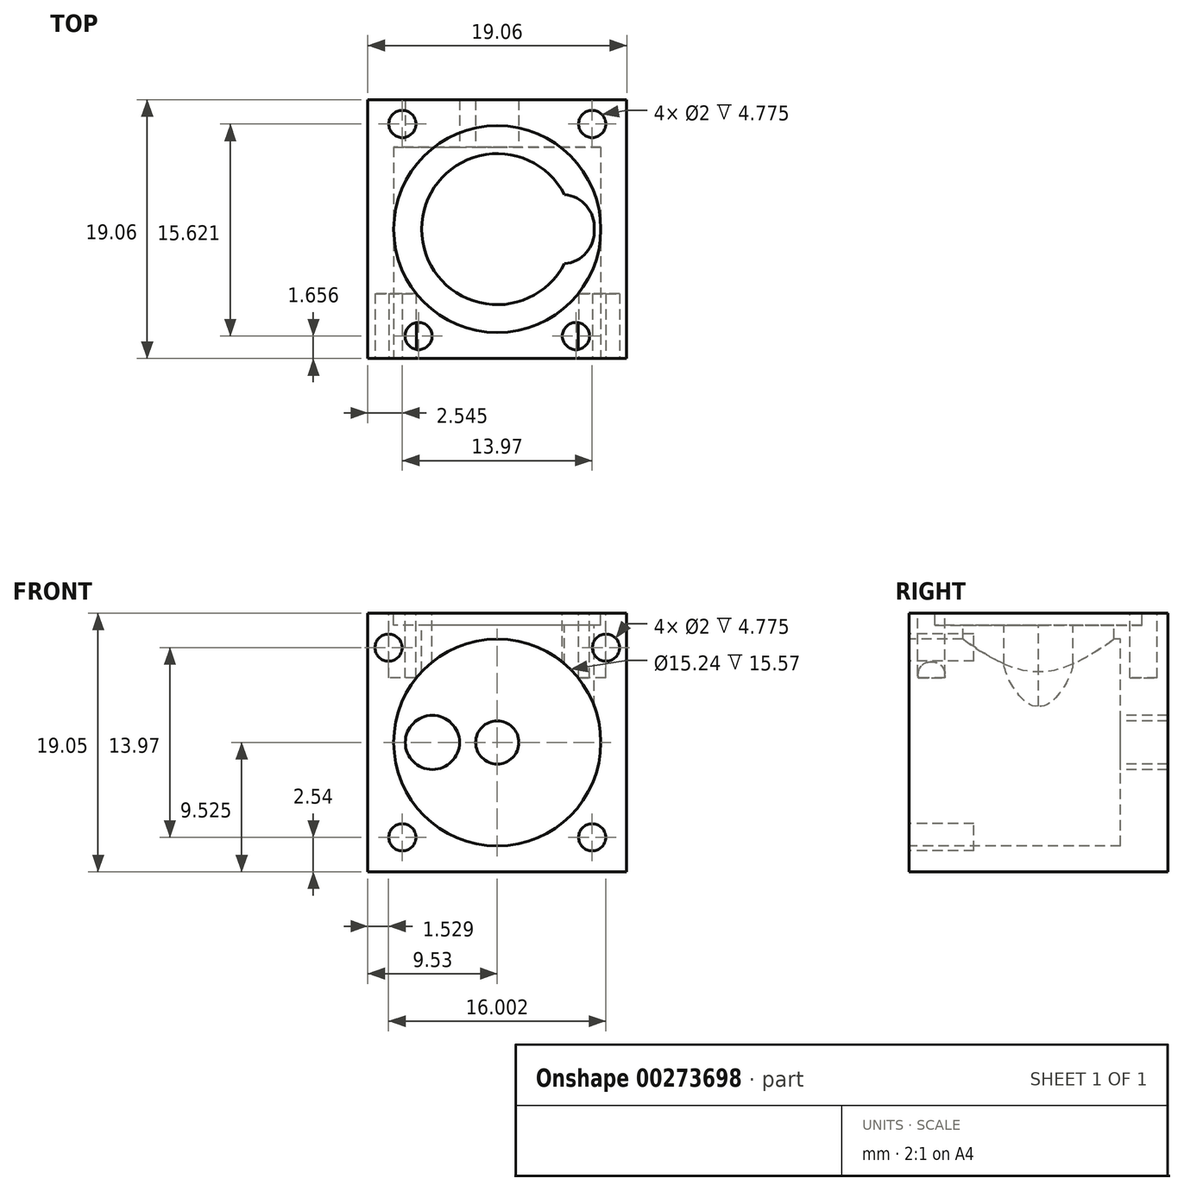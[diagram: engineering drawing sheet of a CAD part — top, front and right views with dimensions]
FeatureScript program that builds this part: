
annotation { "Feature Type Name" : "Feature", "Feature Type Description" : "" }
export const myFeature = defineFeature(function(context is Context, id is Id, definition is map)
    precondition{}
    {
        {
            var Q0;
            Q0=qCreatedBy(makeId("Top.planeOp"),FACE);
            var sketch = newSketch(context, id + "F0", { "sketchPlane" : qUnion([Q0])});
            skLineSegment(sketch, "E0.bottom", {"start": v(9.53, -9.52) * mm, "end": v(-9.53, -9.53) * mm});
            skLineSegment(sketch, "E0.top", {"start": v(9.53, 9.53) * mm, "end": v(-9.53, 9.52) * mm});
            skLineSegment(sketch, "E0.left", {"start": v(9.53, -9.52) * mm, "end": v(9.53, 9.53) * mm});
            skLineSegment(sketch, "E0.right", {"start": v(-9.53, -9.53) * mm, "end": v(-9.53, 9.52) * mm});
            skPoint(sketch, "E0.middle", {"position": v(0, 0) * mm});
            skSolve(sketch);
        }
        {
            var Q0;
            Q0 = qSketchRegion(id + "F0", true);
            extrude(context, id + "F1", {"entities" : qUnion([Q0]), "depth" : 19.05 * mm});
        }
        {
            var Q0;
            Q0=makeQuery(id+"F1.opExtrude","CAP_FACE",FACE,{"disambiguationData":[OSD([sQuery(id+"F0.wireOp",EDGE,"E0.bottom"),sQuery(id+"F0.wireOp",EDGE,"E0.top"),sQuery(id+"F0.wireOp",EDGE,"E0.left"),sQuery(id+"F0.wireOp",EDGE,"E0.right")])],"isStart":false});
            var sketch = newSketch(context, id + "F2", { "sketchPlane" : qUnion([Q0])});
            skCircle(sketch, "E1", {"center": v(0, 0) * mm, "radius": 7.62 * mm});
            skArc(sketch, "E2", {"start": v(4.95, 2.54) * mm, "mid": v(-5.56, 0) * mm, "end": v(4.95, -2.54) * mm});
            skCircle(sketch, "E3", {"center": v(-5.8, -7.87) * mm, "radius": 1 * mm, "construction": true});
            skCircle(sketch, "E4", {"center": v(-6.99, 7.75) * mm, "radius": 1 * mm, "construction": true});
            skCircle(sketch, "E5", {"center": v(5.8, -7.87) * mm, "radius": 1 * mm, "construction": true});
            skCircle(sketch, "E6", {"center": v(6.99, 7.75) * mm, "radius": 1 * mm, "construction": true});
            skArc(sketch, "E7", {"start": v(4.95, -2.54) * mm, "mid": v(6.56, -1.72) * mm, "end": v(7.13, 0) * mm});
            skArc(sketch, "E8", {"start": v(7.13, 0) * mm, "mid": v(6.56, 1.72) * mm, "end": v(4.95, 2.54) * mm});
            skSolve(sketch);
        }
        {
            var Q0;
            Q0 = qSketchRegion(id + "F2", true);
            extrude(context, id + "F3", {"entities" : qUnion([Q0]), "operationType" : NewBodyOperationType.REMOVE, "oppositeDirection" : true, "depth" : 0.89 * mm});
        }
        {
            var Q0;
            Q0=makeQuery(id+"F2.imprint","IMPRINT",FACE,{"disambiguationData":[TD([[makeQuery(id+"F2.imprint","IMPRINT",EDGE,{"derivedFrom":sQuery(id+"F2.wireOp",EDGE,"E1")}),-1.0]])]});
            var sketch = newSketch(context, id + "F4", { "sketchPlane" : qUnion([Q0])});
            skCircle(sketch, "E9.0", {"center": v(-5.8, -7.87) * mm, "radius": 1 * mm});
            skCircle(sketch, "E10.0", {"center": v(5.8, -7.87) * mm, "radius": 1 * mm});
            skCircle(sketch, "E11.0", {"center": v(6.99, 7.75) * mm, "radius": 1 * mm});
            skCircle(sketch, "E12.0", {"center": v(-6.99, 7.75) * mm, "radius": 1 * mm});
            skSolve(sketch);
        }
        {
            var Q0;
            Q0 = qSketchRegion(id + "F4", true);
            extrude(context, id + "F5", {"entities" : qUnion([Q0]), "operationType" : NewBodyOperationType.REMOVE, "oppositeDirection" : true, "depth" : 4.78 * mm});
        }
        {
            var Q0;
            Q0=makeQuery(id+"F1.opExtrude","SWEPT_FACE",FACE,{"disambiguationData":[OSD([sQuery(id+"F0.wireOp",EDGE,"E0.bottom")])]});
            var sketch = newSketch(context, id + "F6", { "sketchPlane" : qUnion([Q0])});
            skLineSegment(sketch, "E13", {"start": v(-9.53, 19.05) * mm, "end": v(9.53, 0) * mm, "construction": true});
            skLineSegment(sketch, "E14", {"start": v(9.53, 19.05) * mm, "end": v(-9.53, 0) * mm, "construction": true});
            skPoint(sketch, "E15", {"position": v(0, 9.53) * mm});
            skCircle(sketch, "E16", {"center": v(0, 9.53) * mm, "radius": 7.62 * mm});
            skSolve(sketch);
        }
        {
            var Q0;
            Q0 = qSketchRegion(id + "F6", true);
            extrude(context, id + "F7", {"entities" : qUnion([Q0]), "operationType" : NewBodyOperationType.REMOVE, "oppositeDirection" : true, "depth" : 15.57 * mm});
        }
        {
            var Q0;
            Q0=makeQuery(id+"F3.boolean.opBoolean","SPLIT",FACE,{"disambiguationData":[TD([makeQuery(id+"F3.opExtrude","SWEPT_FACE",FACE,{"disambiguationData":[OSD([sQuery(id+"F2.wireOp",EDGE,"E2")])]})])],"derivedFrom":makeQuery(id+"F1.opExtrude","CAP_FACE",FACE,{"disambiguationData":[OSD([sQuery(id+"F0.wireOp",EDGE,"E0.bottom"),sQuery(id+"F0.wireOp",EDGE,"E0.top"),sQuery(id+"F0.wireOp",EDGE,"E0.left"),sQuery(id+"F0.wireOp",EDGE,"E0.right")])],"isStart":false})});
            var sketch = newSketch(context, id + "F8", { "sketchPlane" : qUnion([Q0])});
            skArc(sketch, "E17.0.0", {"start": v(4.95, -2.54) * mm, "mid": v(6.56, -1.72) * mm, "end": v(7.13, 0) * mm});
            skArc(sketch, "E17.0.1", {"start": v(7.13, 0) * mm, "mid": v(6.56, 1.72) * mm, "end": v(4.95, 2.54) * mm});
            skArc(sketch, "E17.0.2", {"start": v(4.95, 2.54) * mm, "mid": v(-5.56, 0) * mm, "end": v(4.95, -2.54) * mm});
            skSolve(sketch);
        }
        {
            var Q0;
            Q0 = qSketchRegion(id + "F8", true);
            extrude(context, id + "F9", {"entities" : qUnion([Q0]), "operationType" : NewBodyOperationType.REMOVE, "endBound" : BoundingType.UP_TO_NEXT, "oppositeDirection" : true, "depth" : 25.4 * mm});
        }
        {
            var Q0;
            Q0=makeQuery(id+"F7.boolean.opBoolean","COPY",FACE,{"derivedFrom":makeQuery(id+"F7.opExtrude","CAP_FACE",FACE,{"disambiguationData":[OSD([sQuery(id+"F6.wireOp",EDGE,"E16")])],"isStart":false})});
            var sketch = newSketch(context, id + "F10", { "sketchPlane" : qUnion([Q0])});
            skCircle(sketch, "E18.0", {"center": v(0, 9.53) * mm, "radius": 7.62 * mm, "construction": true});
            skCircle(sketch, "E19", {"center": v(0, 9.53) * mm, "radius": 1.59 * mm});
            skCircle(sketch, "E20", {"center": v(-4.78, 9.53) * mm, "radius": 2 * mm});
            skSolve(sketch);
        }
        {
            var Q0;
            Q0 = qSketchRegion(id + "F10", true);
            extrude(context, id + "F11", {"entities" : qUnion([Q0]), "operationType" : NewBodyOperationType.REMOVE, "endBound" : BoundingType.THROUGH_ALL, "oppositeDirection" : true, "depth" : 25.4 * mm});
        }
        {
            var Q0;
            Q0=makeQuery(id+"F1.opExtrude","SWEPT_FACE",FACE,{"disambiguationData":[OSD([sQuery(id+"F0.wireOp",EDGE,"E0.bottom")])]});
            var sketch = newSketch(context, id + "F12", { "sketchPlane" : qUnion([Q0])});
            skCircle(sketch, "E21", {"center": v(-8, 16.5) * mm, "radius": 1 * mm});
            skCircle(sketch, "E22", {"center": v(8, 16.51) * mm, "radius": 1 * mm});
            skCircle(sketch, "E23", {"center": v(-6.99, 2.54) * mm, "radius": 1 * mm});
            skCircle(sketch, "E24", {"center": v(6.99, 2.54) * mm, "radius": 1 * mm});
            skLineSegment(sketch, "E25", {"start": v(0, 19.05) * mm, "end": v(0, 0) * mm, "construction": true});
            skSolve(sketch);
        }
        {
            var Q0;
            Q0 = qSketchRegion(id + "F12", true);
            extrude(context, id + "F13", {"entities" : qUnion([Q0]), "operationType" : NewBodyOperationType.REMOVE, "oppositeDirection" : true, "depth" : 4.78 * mm});
        }
    });
